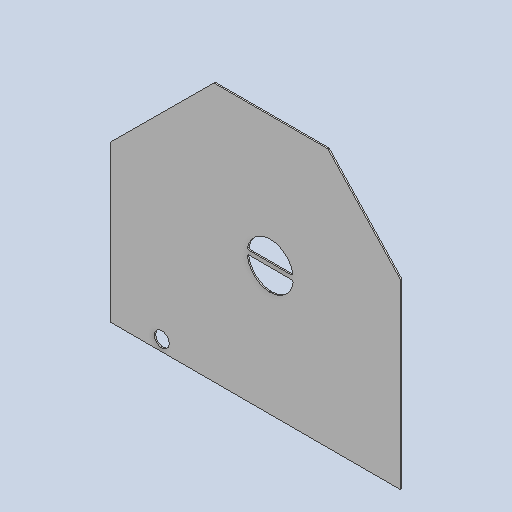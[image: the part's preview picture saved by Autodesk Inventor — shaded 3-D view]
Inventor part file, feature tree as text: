
AUTODESK INVENTOR PART (.ipt)
format: ipt  version: 2025 (Build 290162010, 162A)  size: 249,344 bytes
history: native  units: mm
features: extrude x2, fillet x1, pattern_circular x1, sketch x1, other x1
ambient origin geometry x8: Origin, YZ Plane, XZ Plane, XY Plane, X Axis, Y Axis, Z Axis, Center Point
bodies: Solid1 (feature_tree)
feature tree (6):
  extrude  "Extrusion1"  Depth=780.0mm
  fillet  "Fillet1"  Radius=1180.0mm
  extrude  "Extrusion4"  Depth=950.0mm
  pattern_circular  "Circular Pattern3"  [2 undecoded]
  sketch  "Sketch4"  dims[d1=840.0mm d3=1150.0mm d12=1180.0mm d13=950.0mm d14=111.0mm d15=1910.0mm d17=-521.637743mm d18=377.0mm d19=-269.216713mm d24=10.0mm d25=0.0mm d34=380.0mm d35=80.0mm d37=2140.0mm d52=530.0mm d53=5.0mm d54=10.0mm d55=30.0mm d56=10.0mm d59=265.0mm d60=13.0mm d61=1.963495mm d62=10.0mm d63=0.0mm d64=160.0mm d65=360.0deg d67=5.0mm d68=5.0mm d69=780.0mm d71=1078.0mm d72=340.0mm d70=0.872665mm]
  other  "Definition1"
note: 2 required parameter values undecoded (feature->parameter linkage not recoverable at this tier; creation-order binding heuristic only, values carry confidence <= 0.55)
